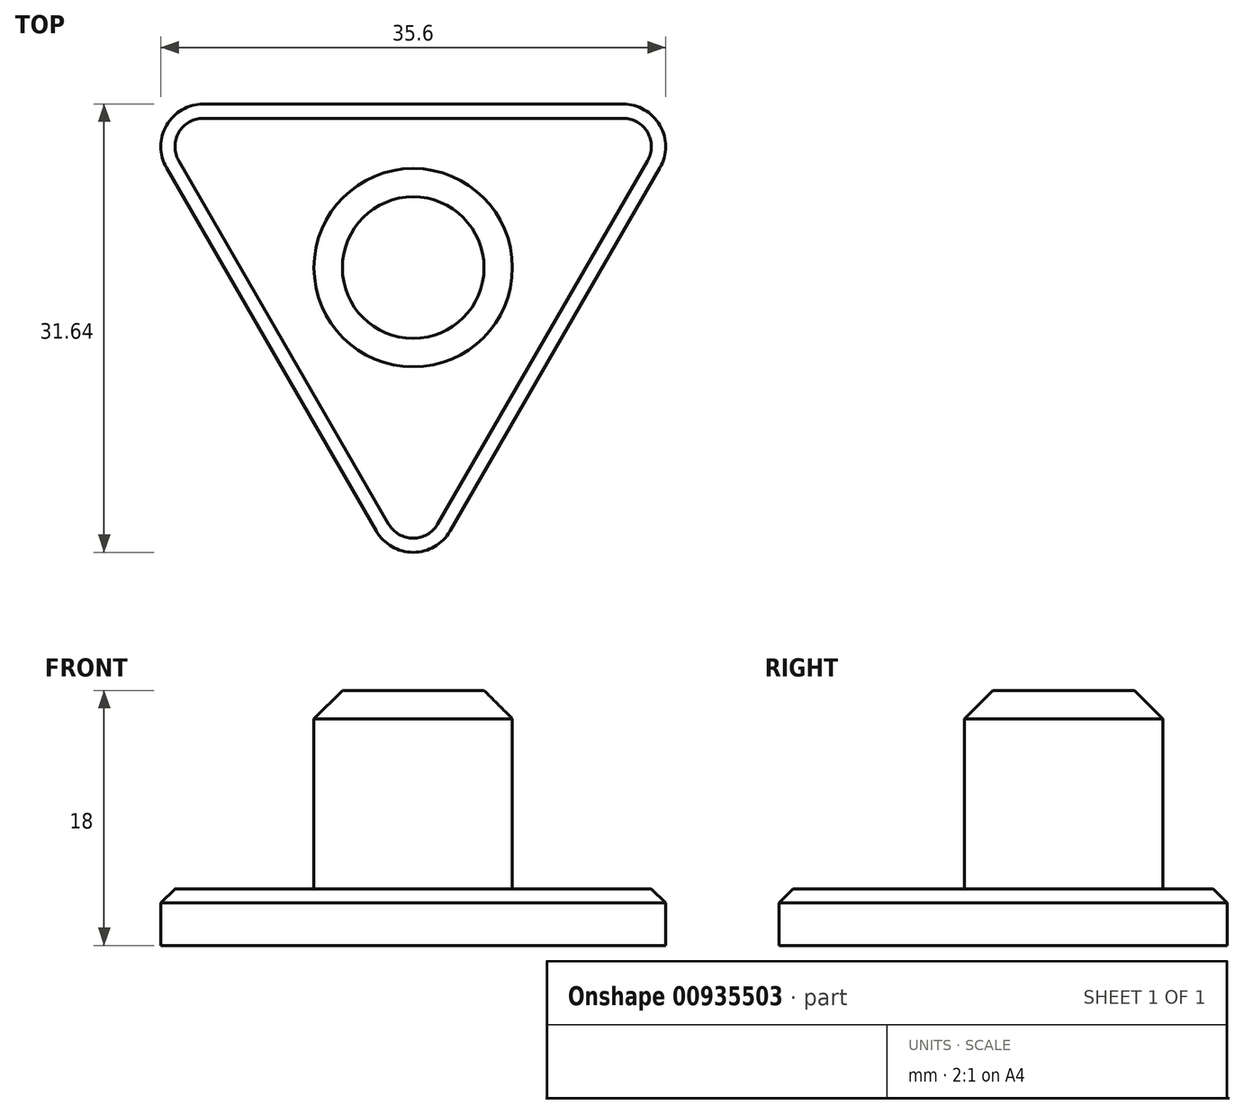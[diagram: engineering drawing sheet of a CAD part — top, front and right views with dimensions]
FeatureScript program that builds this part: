
annotation { "Feature Type Name" : "Feature", "Feature Type Description" : "" }
export const myFeature = defineFeature(function(context is Context, id is Id, definition is map)
    precondition{}
    {
        {
            var Q0;
            Q0=qCreatedBy(makeId("Top.planeOp"),FACE);
            var sketch = newSketch(context, id + "F0", { "sketchPlane" : qUnion([Q0])});
            skLineSegment(sketch, "E0", {"start": v(0, 0) * mm, "end": v(40, 0) * mm});
            skLineSegment(sketch, "E1", {"start": v(40, 0) * mm, "end": v(20, -34.64) * mm});
            skLineSegment(sketch, "E2", {"start": v(20, -34.64) * mm, "end": v(0, 0) * mm});
            skSolve(sketch);
        }
        {
            var Q0;
            Q0=makeQuery(id+"F0.imprint","IMPRINT",FACE,{"disambiguationData":[TD([[makeQuery(id+"F0.imprint","IMPRINT",EDGE,{"derivedFrom":sQuery(id+"F0.wireOp",EDGE,"E0")}),-1.0]])]});
            extrude(context, id + "F1", {"entities" : qUnion([Q0]), "depth" : 4 * mm, "offsetDistance" : 25 * mm});
        }
        {
            var Q0;
            Q0=makeQuery(id+"F1.opExtrude","CAP_FACE",FACE,{"disambiguationData":[OSD([sQuery(id+"F0.wireOp",EDGE,"E0"),sQuery(id+"F0.wireOp",EDGE,"E1"),sQuery(id+"F0.wireOp",EDGE,"E2")])],"isStart":false});
            var sketch = newSketch(context, id + "F2", { "sketchPlane" : qUnion([Q0])});
            skLineSegment(sketch, "E3", {"start": v(20, 0) * mm, "end": v(20, -44.95) * mm, "construction": true});
            skLineSegment(sketch, "E4", {"start": v(40, 0) * mm, "end": v(10, -17.32) * mm, "construction": true});
            skCircle(sketch, "E5", {"center": v(20, -11.55) * mm, "radius": 7 * mm});
            skSolve(sketch);
        }
        {
            var Q0;
            Q0 = qSketchRegion(id + "F2", true);
            extrude(context, id + "F3", {"entities" : qUnion([Q0]), "operationType" : NewBodyOperationType.ADD, "depth" : 14 * mm, "offsetDistance" : 25 * mm});
        }
        {
            var Q0;
            Q0=makeQuery(id+"F1.opExtrude","SWEPT_EDGE",EDGE,{"disambiguationData":[OSD([sQuery(id+"F0.wireOp",EDGE,"E1"),sQuery(id+"F0.wireOp",EDGE,"E2")])]});
            var Q1;
            Q1=makeQuery(id+"F1.opExtrude","SWEPT_EDGE",EDGE,{"disambiguationData":[OSD([sQuery(id+"F0.wireOp",EDGE,"E0"),sQuery(id+"F0.wireOp",EDGE,"E1")])]});
            var Q2;
            Q2=makeQuery(id+"F1.opExtrude","SWEPT_EDGE",EDGE,{"disambiguationData":[OSD([sQuery(id+"F0.wireOp",EDGE,"E0"),sQuery(id+"F0.wireOp",EDGE,"E2")])]});
            fillet(context, id + "F4", {"entities" : qUnion([Q0, Q1, Q2]), "radius" : 3 * mm, "tangentPropagation" : true, "allowEdgeOverflow" : false});
        }
        {
            var Q0;
            Q0=makeQuery(id+"F1.opExtrude","CAP_EDGE",EDGE,{"disambiguationData":[OSD([sQuery(id+"F0.wireOp",EDGE,"E1")])],"isStart":false});
            chamfer(context, id + "F5", {"entities" : qUnion([Q0]), "width" : 1 * mm, "tangentPropagation" : true});
        }
        {
            var Q0;
            Q0=makeQuery(id+"F3.opExtrude","CAP_FACE",FACE,{"disambiguationData":[OSD([sQuery(id+"F2.wireOp",EDGE,"E5")])],"isStart":false});
            var Q1;
            Q1=makeQuery(id+"F3.opExtrude","CAP_EDGE",EDGE,{"disambiguationData":[OSD([sQuery(id+"F2.wireOp",EDGE,"E5")])],"isStart":true});
            chamfer(context, id + "F6", {"entities" : qUnion([Q0, Q1]), "width" : 2 * mm, "tangentPropagation" : true});
        }
    });
